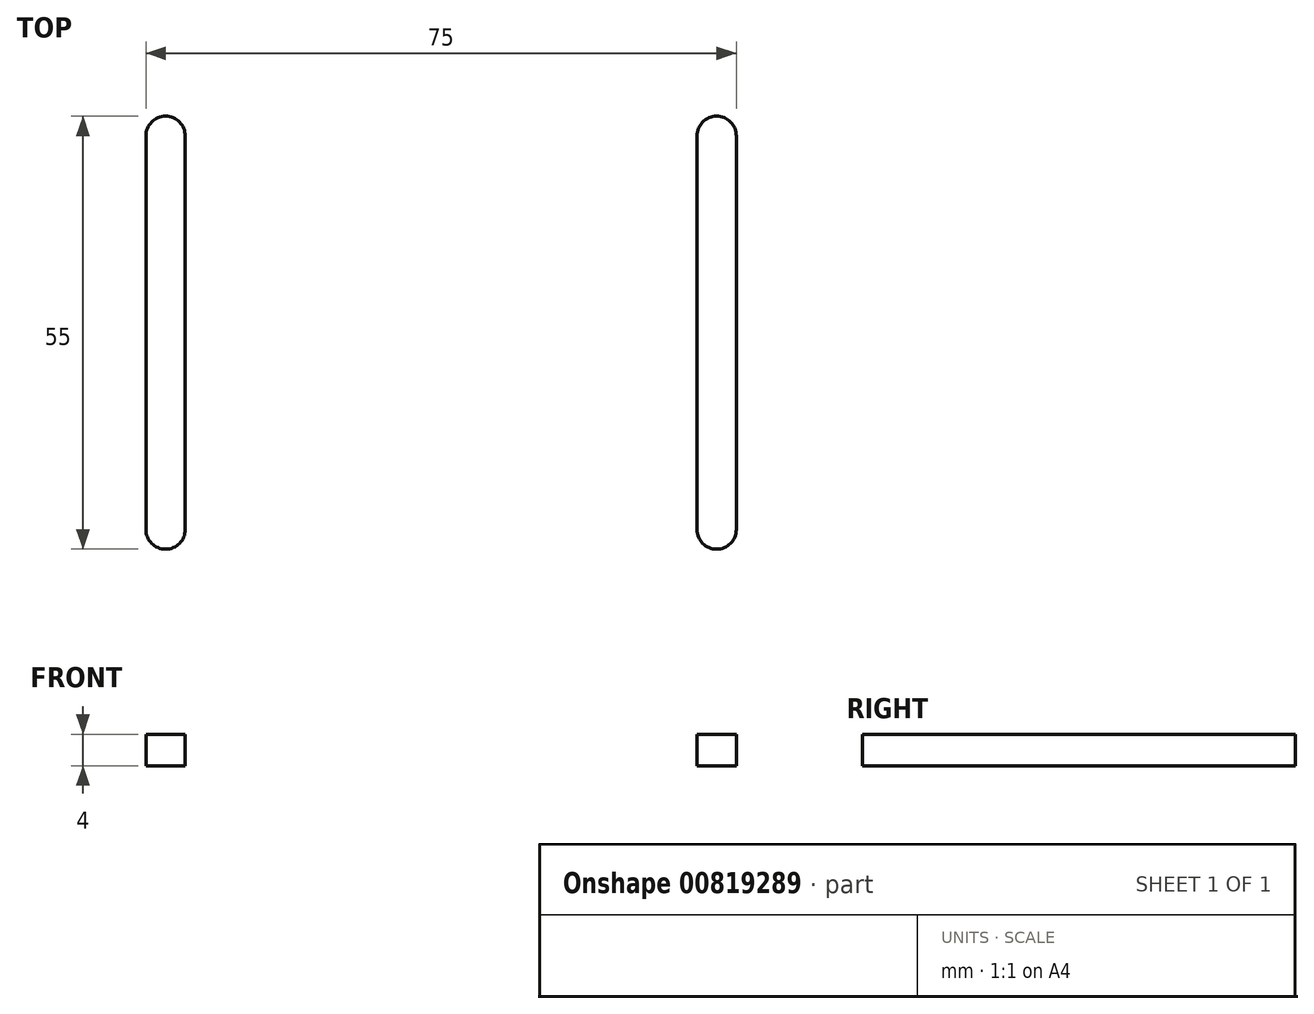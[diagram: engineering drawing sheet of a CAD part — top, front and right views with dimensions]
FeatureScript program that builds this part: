
annotation { "Feature Type Name" : "Feature", "Feature Type Description" : "" }
export const myFeature = defineFeature(function(context is Context, id is Id, definition is map)
    precondition{}
    {
        {
            var Q0;
            Q0=qCreatedBy(makeId("Top.planeOp"),FACE);
            var sketch = newSketch(context, id + "F0", { "sketchPlane" : qUnion([Q0])});
            skLineSegment(sketch, "E0.bottom", {"start": v(0, 0) * mm, "end": v(45, 0) * mm});
            skLineSegment(sketch, "E0.top", {"start": v(0, 135) * mm, "end": v(45, 135) * mm});
            skLineSegment(sketch, "E0.left", {"start": v(0, 0) * mm, "end": v(0, 135) * mm});
            skLineSegment(sketch, "E0.right", {"start": v(45, 0) * mm, "end": v(45, 135) * mm});
            skSolve(sketch);
        }
        {
            var Q0;
            Q0=makeQuery(id+"F0.imprint","IMPRINT",FACE,{"disambiguationData":[TD([[makeQuery(id+"F0.imprint","IMPRINT",EDGE,{"derivedFrom":sQuery(id+"F0.wireOp",EDGE,"E0.bottom")}),1.0]])]});
            extrude(context, id + "F1", {"entities" : qUnion([Q0]), "depth" : 4 * mm, "offsetDistance" : 25 * mm});
        }
        {
            var Q0;
            Q0=makeQuery(id+"F1.opExtrude","SWEPT_EDGE",EDGE,{"disambiguationData":[OSD([sQuery(id+"F0.wireOp",EDGE,"E0.top"),sQuery(id+"F0.wireOp",EDGE,"E0.right")])]});
            chamfer(context, id + "F2", {"entities" : qUnion([Q0]), "width" : 45 * mm, "tangentPropagation" : true});
        }
        {
            var Q0;
            Q0=qCreatedBy(makeId("Top.planeOp"),FACE);
            var sketch = newSketch(context, id + "F3", { "sketchPlane" : qUnion([Q0])});
            skLineSegment(sketch, "E1", {"start": v(35, 20) * mm, "end": v(35, 70) * mm});
            skSolve(sketch);
        }
        {
            var Q0;
            Q0=makeQuery(id+"F1.opExtrude","CAP_FACE",FACE,{"disambiguationData":[OSD([sQuery(id+"F0.wireOp",EDGE,"E0.bottom"),sQuery(id+"F0.wireOp",EDGE,"E0.top"),sQuery(id+"F0.wireOp",EDGE,"E0.left"),sQuery(id+"F0.wireOp",EDGE,"E0.right")])],"isStart":false});
            var sketch = newSketch(context, id + "F4", { "sketchPlane" : qUnion([Q0])});
            skLineSegment(sketch, "E2.JUB.JUB", {"start": v(35, 20) * mm, "end": v(35, 70) * mm, "construction": true});
            skArc(sketch, "E2.0.startCap", {"start": v(37.5, 20) * mm, "mid": v(35, 17.5) * mm, "end": v(32.5, 20) * mm});
            skArc(sketch, "E2.0.endCap", {"start": v(32.5, 70) * mm, "mid": v(35, 72.5) * mm, "end": v(37.5, 70) * mm});
            skLineSegment(sketch, "E2.0.left", {"start": v(32.5, 20) * mm, "end": v(32.5, 70) * mm});
            skLineSegment(sketch, "E2.0.right", {"start": v(37.5, 20) * mm, "end": v(37.5, 70) * mm});
            skSolve(sketch);
        }
        {
            var Q0;
            Q0=makeQuery(id+"F4.imprint","IMPRINT",FACE,{"disambiguationData":[TD([[makeQuery(id+"F4.imprint","IMPRINT",EDGE,{"derivedFrom":sQuery(id+"F4.wireOp",EDGE,"E2.0.startCap")}),-1.0]])]});
            extrude(context, id + "F5", {"entities" : qUnion([Q0]), "operationType" : NewBodyOperationType.REMOVE, "oppositeDirection" : true, "depth" : 39.12 * mm, "offsetDistance" : 25 * mm});
        }
        {
            var Q0;
            {var subQ0=makeQuery(id+"F1.opExtrude","CAP_FACE",FACE,{"disambiguationData":[OSD([sQuery(id+"F0.wireOp",EDGE,"E0.bottom"),sQuery(id+"F0.wireOp",EDGE,"E0.top"),sQuery(id+"F0.wireOp",EDGE,"E0.left"),sQuery(id+"F0.wireOp",EDGE,"E0.right")])],"isStart":false});Q0=makeQuery(id+"FC9QmeRWRDP4uqh_1.boolean.opBoolean","MERGE",FACE,{"derivedFrom":[subQ0,makeQuery(id+"FC9QmeRWRDP4uqh_1.opPattern","COPY",FACE,{"derivedFrom":subQ0,"instanceName":"1"})]});}
            var sketch = newSketch(context, id + "F6", { "sketchPlane" : qUnion([Q0])});
            skLineSegment(sketch, "E3", {"start": v(15.9, 0) * mm, "end": v(16.58, 7.97) * mm});
            skSolve(sketch);
        }
        {
            var Q0;
            Q0=sQuery(id+"F6.wireOp",VERTEX,"E3.end");
            var Q1;
            Q1=makeQuery(id+"F1.opExtrude","SWEPT_BODY",BODY,{"disambiguationData":[OSD([sQuery(id+"F0.wireOp",EDGE,"E0.bottom"),sQuery(id+"F0.wireOp",EDGE,"E0.top"),sQuery(id+"F0.wireOp",EDGE,"E0.left"),sQuery(id+"F0.wireOp",EDGE,"E0.right")])]});
            hole(context, id + "F7", {"style" : HoleStyle.SIMPLE, "endStyle" : HoleEndStyle.THROUGH, "holeDiameter" : 3 * mm, "majorDiameter" : 5 * mm, "isTappedThrough" : true, "tappedDepth" : 12 * mm, "tapClearance" : 3, "locations" : qUnion([Q0]), "scope" : qUnion([Q1])});
        }
        {
            var Q0;
            {var subQ0=makeQuery(id+"F1.opExtrude","CAP_FACE",FACE,{"disambiguationData":[OSD([sQuery(id+"F0.wireOp",EDGE,"E0.bottom"),sQuery(id+"F0.wireOp",EDGE,"E0.top"),sQuery(id+"F0.wireOp",EDGE,"E0.left"),sQuery(id+"F0.wireOp",EDGE,"E0.right")])],"isStart":false});Q0=makeQuery(id+"FC9QmeRWRDP4uqh_1.boolean.opBoolean","MERGE",FACE,{"derivedFrom":[subQ0,makeQuery(id+"FC9QmeRWRDP4uqh_1.opPattern","COPY",FACE,{"derivedFrom":subQ0,"instanceName":"1"})]});}
            var sketch = newSketch(context, id + "F8", { "sketchPlane" : qUnion([Q0])});
            skLineSegment(sketch, "E4", {"start": v(35, 0) * mm, "end": v(35, 17.5) * mm});
            skPoint(sketch, "E4.startSnap0", {"position": v(35, 17.5) * mm});
            skLineSegment(sketch, "E5", {"start": v(25, 0) * mm, "end": v(45, 0) * mm});
            skLineSegment(sketch, "E6", {"start": v(25, 0) * mm, "end": v(25, 30.5) * mm});
            skSolve(sketch);
        }
        {
            var Q0;
            Q0=sQuery(id+"F8.wireOp",VERTEX,"E6.end");
            var Q1;
            Q1=makeQuery(id+"F1.opExtrude","SWEPT_BODY",BODY,{"disambiguationData":[OSD([sQuery(id+"F0.wireOp",EDGE,"E0.bottom"),sQuery(id+"F0.wireOp",EDGE,"E0.top"),sQuery(id+"F0.wireOp",EDGE,"E0.left"),sQuery(id+"F0.wireOp",EDGE,"E0.right")])]});
            hole(context, id + "F9", {"style" : HoleStyle.SIMPLE, "endStyle" : HoleEndStyle.THROUGH, "holeDiameter" : 3 * mm, "majorDiameter" : 5 * mm, "isTappedThrough" : true, "tappedDepth" : 12 * mm, "tapClearance" : 3, "locations" : qUnion([Q0]), "scope" : qUnion([Q1])});
        }
        {
            var Q0;
            Q0=makeQuery(id+"F1.opExtrude","CAP_FACE",FACE,{"disambiguationData":[OSD([sQuery(id+"F0.wireOp",EDGE,"E0.bottom"),sQuery(id+"F0.wireOp",EDGE,"E0.top"),sQuery(id+"F0.wireOp",EDGE,"E0.left"),sQuery(id+"F0.wireOp",EDGE,"E0.right")])],"isStart":false});
            var sketch = newSketch(context, id + "F10", { "sketchPlane" : qUnion([Q0])});
            skLineSegment(sketch, "E7", {"start": v(25, 30.5) * mm, "end": v(25, 54.5) * mm});
            skSolve(sketch);
        }
        {
            var Q0;
            Q0=sQuery(id+"F10.wireOp",VERTEX,"E7.end");
            var Q1;
            Q1=makeQuery(id+"F1.opExtrude","SWEPT_BODY",BODY,{"disambiguationData":[OSD([sQuery(id+"F0.wireOp",EDGE,"E0.bottom"),sQuery(id+"F0.wireOp",EDGE,"E0.top"),sQuery(id+"F0.wireOp",EDGE,"E0.left"),sQuery(id+"F0.wireOp",EDGE,"E0.right")])]});
            hole(context, id + "F11", {"style" : HoleStyle.SIMPLE, "endStyle" : HoleEndStyle.THROUGH, "holeDiameter" : 3 * mm, "majorDiameter" : 5 * mm, "isTappedThrough" : true, "tappedDepth" : 12 * mm, "tapClearance" : 3, "locations" : qUnion([Q0]), "scope" : qUnion([Q1])});
        }
        {
            var Q0;
            Q0=makeQuery(id+"F1.opExtrude","SWEPT_BODY",BODY,{"disambiguationData":[OSD([sQuery(id+"F0.wireOp",EDGE,"E0.bottom"),sQuery(id+"F0.wireOp",EDGE,"E0.top"),sQuery(id+"F0.wireOp",EDGE,"E0.left"),sQuery(id+"F0.wireOp",EDGE,"E0.right")])]});
            var Q1;
            Q1=qCreatedBy(makeId("Right.planeOp"),FACE);
            mirror(context, id + "F12", {"operationType" : NewBodyOperationType.ADD, "entities" : qUnion([Q0]), "mirrorPlane" : qUnion([Q1])});
        }
        {
            var Q0;
            {var subQ0=makeQuery(id+"F1.opExtrude","CAP_FACE",FACE,{"disambiguationData":[OSD([sQuery(id+"F0.wireOp",EDGE,"E0.bottom"),sQuery(id+"F0.wireOp",EDGE,"E0.top"),sQuery(id+"F0.wireOp",EDGE,"E0.left"),sQuery(id+"F0.wireOp",EDGE,"E0.right")])],"isStart":false});Q0=makeQuery(id+"F12.boolean.opBoolean","MERGE",FACE,{"derivedFrom":[subQ0,makeQuery(id+"F12.opPattern","COPY",FACE,{"derivedFrom":subQ0,"instanceName":"1"})]});}
            var sketch = newSketch(context, id + "F13", { "sketchPlane" : qUnion([Q0])});
            skLineSegment(sketch, "E8", {"start": v(-9.62, 118.53) * mm, "end": v(8.38, 118.53) * mm});
            skSolve(sketch);
        }
        {
            var Q0;
            Q0=sQuery(id+"F13.wireOp",VERTEX,"E8.start");
            var Q1;
            Q1=sQuery(id+"F13.wireOp",VERTEX,"E8.end");
            var Q2;
            Q2=makeQuery(id+"F1.opExtrude","SWEPT_BODY",BODY,{"disambiguationData":[OSD([sQuery(id+"F0.wireOp",EDGE,"E0.bottom"),sQuery(id+"F0.wireOp",EDGE,"E0.top"),sQuery(id+"F0.wireOp",EDGE,"E0.left"),sQuery(id+"F0.wireOp",EDGE,"E0.right")])]});
            hole(context, id + "F14", {"style" : HoleStyle.SIMPLE, "endStyle" : HoleEndStyle.THROUGH, "holeDiameter" : 3 * mm, "majorDiameter" : 5 * mm, "isTappedThrough" : true, "tappedDepth" : 12 * mm, "tapClearance" : 3, "locations" : qUnion([Q0, Q1]), "scope" : qUnion([Q2])});
        }
    });
